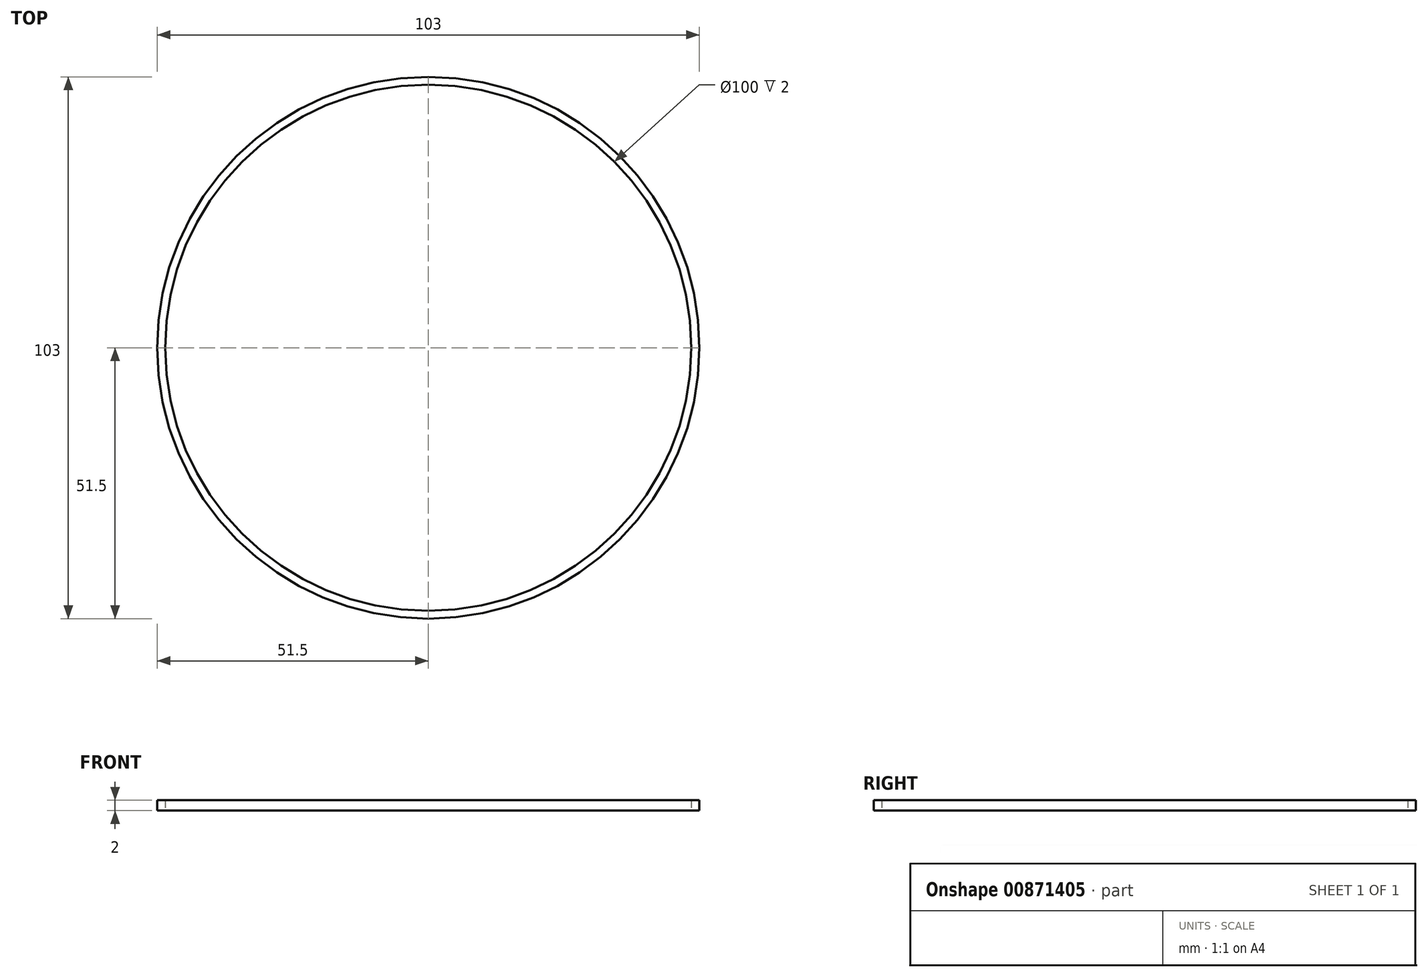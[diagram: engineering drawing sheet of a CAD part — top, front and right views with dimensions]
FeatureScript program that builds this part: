
annotation { "Feature Type Name" : "Feature", "Feature Type Description" : "" }
export const myFeature = defineFeature(function(context is Context, id is Id, definition is map)
    precondition{}
    {
        {
            var Q0;
            Q0=qCreatedBy(makeId("Top.planeOp"),FACE);
            var sketch = newSketch(context, id + "F0", { "sketchPlane" : qUnion([Q0])});
            skCircle(sketch, "E0", {"center": v(0, 0) * mm, "radius": 51.5 * mm});
            skCircle(sketch, "E1", {"center": v(0, 0) * mm, "radius": 50 * mm});
            skLineSegment(sketch, "E2", {"start": v(0, 0) * mm, "end": v(0, -50) * mm, "construction": true});
            skLineSegment(sketch, "E3", {"start": v(-2.5, -49.94) * mm, "end": v(-2.5, -30) * mm});
            skLineSegment(sketch, "E4.MirrorCS", {"start": v(2.5, -49.94) * mm, "end": v(2.5, -30) * mm});
            skSolve(sketch);
        }
        {
            var Q0;
            Q0 = qSketchRegion(id + "F0", true);
            extrude(context, id + "F1", {"entities" : qUnion([Q0]), "depth" : 2 * mm, "offsetDistance" : 25 * mm});
        }
    });
